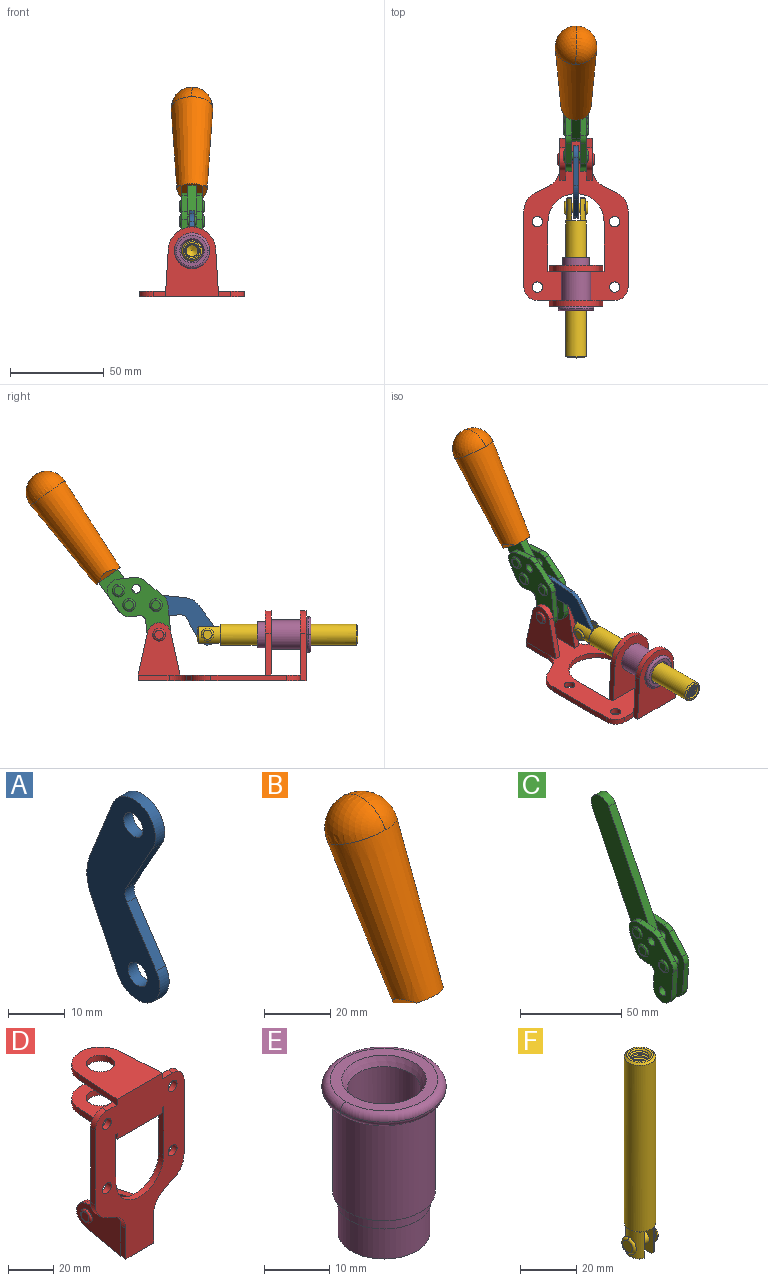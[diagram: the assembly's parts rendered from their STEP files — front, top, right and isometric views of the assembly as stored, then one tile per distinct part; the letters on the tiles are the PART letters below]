
ASSEMBLY  parts=6 mates=6
PART A: 12 faces, bbox 2.3x18.2x42.8 mm
  f0: cylinder r=2.4mm len=4.8mm, axis (1,0,0), area 34.9mm2, adj f4,f11
  f1: cylinder r=10.41mm len=8.47mm, axis (1,0,0), area 20.2mm2, adj f4,f9,f10,f11
  f2: cylinder r=3.05mm len=3.16mm, axis (1,0,0), area 7.7mm2, adj f4,f6,f7,f11
  f3: cylinder r=2.4mm len=4.8mm, axis (1,0,0), area 34.9mm2, adj f4,f11
  f4: plane 42.81x18.23mm, normal (-1,0,0), area 414.1mm2, adj f0,f1,f2,f3,f5,f6,f7,f8
  f5: cylinder r=5.54mm len=10.67mm, axis (1,0,0), area 41.8mm2, adj f4,f6,f10,f11
  f6: plane 11.66x6.53mm, normal (0,-0.87,-0.49), area 30.9mm2, adj f2,f4,f5,f11
  f7: plane 11.17x7.33mm, normal (0,-0.84,0.55), area 30.9mm2, adj f2,f4,f8,f11
  f8: cylinder r=5.54mm len=10.51mm, axis (1,0,0), area 41.8mm2, adj f4,f7,f9,f11
  f9: plane 13.67x6.67mm, normal (0,0.9,-0.44), area 35.1mm2, adj f1,f4,f8,f11
  f10: plane 14.1x5.7mm, normal (0,0.93,0.37), area 35.1mm2, adj f1,f4,f5,f11
  f11: plane 42.81x18.23mm, normal (1,0,0), area 414.1mm2, adj f0,f1,f2,f3,f5,f6,f7,f8
PART B: 11 faces, bbox 22.3x42.6x64.5 mm
  f0: sphere r=11.13mm, area 411.4mm2, adj f1,f8
  f1: cone r=11.11mm half-angle=3.3deg, axis (0,0.44,0.9), area 3251.8mm2, adj f0,f7,f8,f9,f10
  f2: cylinder r=6.16mm len=11.7mm, axis (1,0,0), area 89.5mm2, adj f3,f4,f5,f6
  f3: plane 60.23x36.75mm, normal (-1,0,0), area 763.6mm2, adj f2,f4,f6,f10
  f4: plane 51.37x25.05mm, normal (0,0.9,-0.44), area 264.2mm2, adj f2,f3,f5,f10
  f5: plane 60.23x36.75mm, normal (1,0,0), area 763.6mm2, adj f2,f4,f6,f10
  f6: plane 51.37x25.05mm, normal (0,-0.9,0.44), area 264.2mm2, adj f2,f3,f5,f10
  f7: plane 9.95x5.95mm, normal (0.71,-0.31,-0.64), area 25.8mm2, adj f1,f10
  f8: sphere r=11.13mm, area 411.4mm2, adj f0,f1
  f9: plane 9.95x5.95mm, normal (-0.71,-0.31,-0.64), area 25.8mm2, adj f1,f10
  f10: plane 14.27x11.38mm, normal (0,-0.44,-0.9), area 106.7mm2, adj f1,f3,f4,f5,f6,f7,f9
PART C: 59 faces, bbox 12.9x60.2x99.6 mm
  f0: torus R=2.39mm, axis (-1,0,0), area 14.9mm2, adj f20,f43,f51
  f1: torus R=2.39mm, axis (-1,0,0), area 14.9mm2, adj f19,f42,f51
  f2: torus R=2.39mm, axis (-1,0,0), area 14.9mm2, adj f18,f35,f51
  f3: torus R=2.39mm, axis (-1,0,0), area 14.9mm2, adj f14,f17,f23
  f4: torus R=2.39mm, axis (-1,0,0), area 14.9mm2, adj f13,f16,f23
  f5: torus R=2.39mm, axis (-1,0,0), area 14.9mm2, adj f12,f15,f23
  f6: cylinder r=2.39mm len=4.78mm, axis (1,0,0), area 46.5mm2, adj f48,f50,f51
  f7: cylinder r=2.39mm len=4.78mm, axis (1,0,0), area 46.5mm2, adj f50,f51
  f8: cylinder r=6.35mm len=12.68mm, axis (1,0,0), area 61.8mm2, adj f38,f39,f50,f51
  f9: cylinder r=2.39mm len=4.78mm, axis (-1,0,0), area 70.5mm2, adj f46,f50
  f10: cylinder r=2.39mm len=4.78mm, axis (-1,0,0), area 46.5mm2, adj f23,f45,f46
  f11: cylinder r=2.39mm len=4.78mm, axis (-1,0,0), area 46.5mm2, adj f23,f46
  f12: plane 4.78x4.78mm, normal (1,0,0), area 17.9mm2, adj f5,f15
  f13: plane 4.78x4.78mm, normal (1,0,0), area 17.9mm2, adj f4,f16
  f14: plane 4.78x4.78mm, normal (1,0,0), area 17.9mm2, adj f3,f17
  f15: torus R=2.39mm, axis (-1,0,0), area 14.9mm2, adj f5,f12,f23
  f16: torus R=2.39mm, axis (-1,0,0), area 14.9mm2, adj f4,f13,f23
  f17: torus R=2.39mm, axis (-1,0,0), area 14.9mm2, adj f3,f14,f23
  f18: plane 4.78x4.78mm, normal (-1,0,0), area 17.9mm2, adj f2,f35
  f19: plane 4.78x4.78mm, normal (-1,0,0), area 17.9mm2, adj f1,f42
  f20: plane 4.78x4.78mm, normal (-1,0,0), area 17.9mm2, adj f0,f43
  f21: plane 2.26x0.2mm, normal (1,0,0), area 0.2mm2, adj f31,f44
  f22: plane 2.26x0.2mm, normal (-1,0,0), area 0.2mm2, adj f41,f44
  f23: plane 39.37x30.77mm, normal (1,0,0), area 565.5mm2, adj f3,f4,f5,f10,f11,f15,f16,f17
  f24: cylinder r=6.1mm len=4.15mm, axis (-1,0,0), area 14.7mm2, adj f23,f25,f32,f46
  f25: plane 10.25x9.01mm, normal (0,-0.75,0.66), area 42.3mm2, adj f23,f24,f26,f46
  f26: cylinder r=6.35mm len=4.64mm, axis (-1,0,0), area 15.6mm2, adj f23,f25,f27,f46
  f27: plane 15.84x3.1mm, normal (0,-1,-0.07), area 49.2mm2, adj f23,f26,f28,f46
  f28: cylinder r=6.35mm len=12.68mm, axis (-1,0,0), area 61.8mm2, adj f23,f27,f29,f46
  f29: plane 8.11x3.1mm, normal (0,1,0.07), area 25.2mm2, adj f23,f28,f30,f46
  f30: cylinder r=3.05mm len=3.25mm, axis (-1,0,0), area 14.8mm2, adj f23,f29,f31,f46
  f31: plane 5.99x3.1mm, normal (0,0.07,-1), area 18.6mm2, adj f21,f23,f30,f44,f46
  f32: plane 9.5x3.1mm, normal (0,-0.07,1), area 29.5mm2, adj f23,f24,f33,f46,f47
  f33: cylinder r=6.1mm len=8.63mm, axis (-1,0,0), area 39.1mm2, adj f23,f32,f34,f47
  f34: plane 8.65x3.96mm, normal (0,0.91,-0.42), area 29.5mm2, adj f23,f33,f44,f47
  f35: torus R=2.39mm, axis (-1,0,0), area 14.9mm2, adj f2,f18,f51
  f36: plane 10.25x9.01mm, normal (0,-0.75,0.66), area 42.3mm2, adj f37,f49,f50,f51
  f37: cylinder r=6.35mm len=4.64mm, axis (1,0,0), area 15.6mm2, adj f36,f38,f50,f51
  f38: plane 15.84x3.1mm, normal (0,-1,-0.07), area 49.2mm2, adj f8,f37,f50,f51
  f39: plane 8.11x3.1mm, normal (0,1,0.07), area 25.2mm2, adj f8,f40,f50,f51
  f40: cylinder r=3.05mm len=3.25mm, axis (1,0,0), area 14.8mm2, adj f39,f41,f50,f51
  f41: plane 5.99x3.1mm, normal (0,0.07,-1), area 18.6mm2, adj f22,f40,f44,f50,f51
  f42: torus R=2.39mm, axis (-1,0,0), area 14.9mm2, adj f1,f19,f51
  f43: torus R=2.39mm, axis (-1,0,0), area 14.9mm2, adj f0,f20,f51
  f44: cylinder r=6.35mm len=12.12mm, axis (-1,0,0), area 128.9mm2, adj f21,f22,f23,f31,f34,f41,f46,f47
  f45: plane 2.65x1.35mm, normal (1,0,0), area 1mm2, adj f10,f55
  f46: plane 39.08x20.42mm, normal (-1,0,0), area 412.5mm2, adj f9,f10,f11,f24,f25,f26,f27,f28
  f47: plane 77.62x39.82mm, normal (1,0,0), area 850mm2, adj f32,f33,f34,f44,f53,f54,f55
  f48: plane 2.65x1.35mm, normal (-1,0,0), area 1mm2, adj f6,f55
  f49: cylinder r=6.1mm len=4.15mm, axis (1,0,0), area 14.7mm2, adj f36,f50,f51,f56
  f50: plane 39.08x20.42mm, normal (1,0,0), area 412.5mm2, adj f6,f7,f8,f9,f36,f37,f38,f39
  f51: plane 39.37x30.77mm, normal (-1,0,0), area 565.5mm2, adj f0,f1,f2,f6,f7,f8,f35,f36
  f52: plane 8.65x3.96mm, normal (0,0.91,-0.42), area 29.5mm2, adj f44,f51,f57,f58
  f53: plane 68.49x33.4mm, normal (0,0.9,-0.44), area 358.1mm2, adj f44,f47,f54,f58
  f54: cylinder r=6.35mm len=12.06mm, axis (1,0,0), area 93.7mm2, adj f47,f53,f55,f58
  f55: plane 68.49x33.4mm, normal (0,-0.9,0.44), area 358.1mm2, adj f44,f45,f46,f47,f48,f50,f54,f58
  f56: plane 9.5x3.1mm, normal (0,-0.07,1), area 29.5mm2, adj f49,f50,f51,f57,f58
  f57: cylinder r=6.1mm len=8.63mm, axis (1,0,0), area 39.1mm2, adj f51,f52,f56,f58
  f58: plane 77.62x39.82mm, normal (-1,0,0), area 850mm2, adj f44,f52,f53,f54,f55,f56,f57
PART D: 55 faces, bbox 55.7x37.4x89.8 mm
  f0: torus R=2.41mm, axis (-1,0,0), area 15mm2, adj f11,f15,f25
  f1: torus R=2.41mm, axis (-1,0,0), area 15mm2, adj f10,f12,f22
  f2: cylinder r=2.78mm len=5.56mm, axis (0,-1,0), area 54.2mm2, adj f30,f54
  f3: cylinder r=14.99mm len=29.97mm, axis (0,-1,0), area 145.9mm2, adj f30,f49,f53,f54
  f4: cylinder r=2.78mm len=5.56mm, axis (0,-1,0), area 54.2mm2, adj f30,f54
  f5: cylinder r=2.78mm len=5.56mm, axis (0,-1,0), area 54.2mm2, adj f30,f54
  f6: cylinder r=2.78mm len=5.56mm, axis (0,-1,0), area 54.2mm2, adj f30,f54
  f7: cylinder r=6.35mm len=12.7mm, axis (0,0,1), area 123.6mm2, adj f27,f51
  f8: cylinder r=6.35mm len=12.7mm, axis (0,0,-1), area 124.7mm2, adj f21,f35
  f9: cylinder r=2.41mm len=11.18mm, axis (-1,0,0), area 169.4mm2, adj f16,f19
  f10: plane 4.83x4.83mm, normal (1,0,0), area 18.3mm2, adj f1,f12
  f11: plane 4.83x4.83mm, normal (-1,0,0), area 18.3mm2, adj f0,f15
  f12: torus R=2.41mm, axis (-1,0,0), area 15mm2, adj f1,f10,f22
  f13: cylinder r=6.35mm len=12.41mm, axis (1,0,0), area 53.4mm2, adj f18,f19,f22,f23
  f14: cylinder r=6.35mm len=12.41mm, axis (-1,0,0), area 53.4mm2, adj f16,f17,f24,f25
  f15: torus R=2.41mm, axis (-1,0,0), area 15mm2, adj f0,f11,f25
  f16: plane 27.86x22.35mm, normal (1,0,0), area 425.4mm2, adj f9,f14,f17,f24,f30
  f17: plane 22.86x4.97mm, normal (0,0.21,0.98), area 72.5mm2, adj f14,f16,f25,f30
  f18: plane 22.86x4.97mm, normal (0,0.21,0.98), area 72.5mm2, adj f13,f19,f22,f30
  f19: plane 27.86x22.35mm, normal (-1,0,0), area 425.4mm2, adj f9,f13,f18,f23,f30
  f20: cylinder r=12.7mm len=25.35mm, axis (0,0,-1), area 119.8mm2, adj f21,f34,f35,f36
  f21: plane 34.21x28.07mm, normal (0,0,-1), area 702.4mm2, adj f8,f20,f30,f34,f36
  f22: plane 27.96x22.45mm, normal (1,0,0), area 407.2mm2, adj f1,f12,f13,f18,f23,f30,f42,f43
  f23: plane 22.86x4.97mm, normal (0,0.21,-0.98), area 72.5mm2, adj f13,f19,f22,f44
  f24: plane 22.86x4.97mm, normal (0,0.21,-0.98), area 72.5mm2, adj f14,f16,f25,f44
  f25: plane 27.86x22.35mm, normal (-1,0,0), area 407.1mm2, adj f0,f14,f15,f17,f24,f30,f45,f46
  f26: plane 3.1x0.95mm, normal (0,0,-1), area 2.7mm2, adj f30,f49,f50,f54
  f27: plane 34.21x28.07mm, normal (0,0,1), area 702.4mm2, adj f7,f28,f30,f50,f52
  f28: cylinder r=12.7mm len=25.35mm, axis (0,0,1), area 118.8mm2, adj f27,f50,f51,f52
  f29: plane 3.1x0.95mm, normal (0,0,-1), area 2.7mm2, adj f30,f52,f53,f54
  f30: plane 86.54x55.63mm, normal (0,1,0), area 2362.9mm2, adj f2,f3,f4,f5,f6,f16,f17,f18
  f31: plane 40.56x3.1mm, normal (-1,0,0), area 125.7mm2, adj f30,f32,f48,f54
  f32: cylinder r=7.11mm len=7.11mm, axis (0,-1,0), area 34.6mm2, adj f30,f31,f33,f54
  f33: plane 6.67x3.1mm, normal (0,0,1), area 20.4mm2, adj f30,f32,f34,f54
  f34: plane 25.39x3.13mm, normal (-1,0.06,0), area 79.5mm2, adj f20,f21,f33,f35,f54
  f35: plane 37.31x28.45mm, normal (0,0,1), area 789.9mm2, adj f8,f20,f34,f36,f54
  f36: plane 25.39x3.13mm, normal (1,0.06,0), area 79.5mm2, adj f20,f21,f35,f37,f54
  f37: plane 6.67x3.1mm, normal (0,0,1), area 20.4mm2, adj f30,f36,f38,f54
  f38: cylinder r=7.11mm len=7.11mm, axis (0,-1,0), area 34.6mm2, adj f30,f37,f39,f54
  f39: plane 40.56x3.1mm, normal (1,0,0), area 125.7mm2, adj f30,f38,f40,f54
  f40: cylinder r=11.18mm len=10.16mm, axis (0,-1,0), area 39.5mm2, adj f30,f39,f41,f54
  f41: plane 6.09x3.1mm, normal (0.42,0,-0.91), area 20.8mm2, adj f30,f40,f42,f54
  f42: cylinder r=11.18mm len=9.41mm, axis (0,-1,0), area 37.2mm2, adj f22,f30,f41,f43,f54
  f43: plane 16.5x3.1mm, normal (1,0,0), area 51.1mm2, adj f22,f42,f44,f54
  f44: plane 17.37x3.1mm, normal (0,0,-1), area 53.8mm2, adj f23,f24,f30,f43,f45,f54
  f45: plane 16.5x3.1mm, normal (-1,0,0), area 51.1mm2, adj f25,f44,f46,f54
  f46: cylinder r=11.18mm len=9.41mm, axis (0,-1,0), area 37.2mm2, adj f25,f30,f45,f47,f54
  f47: plane 6.09x3.1mm, normal (-0.42,0,-0.91), area 20.8mm2, adj f30,f46,f48,f54
  f48: cylinder r=11.18mm len=10.16mm, axis (0,-1,0), area 39.5mm2, adj f30,f31,f47,f54
  f49: plane 26.54x3.1mm, normal (-1,0,0), area 82.3mm2, adj f3,f26,f30,f54
  f50: plane 25.39x3.1mm, normal (1,0.06,0), area 78.8mm2, adj f26,f27,f28,f51,f54
  f51: plane 37.31x28.45mm, normal (0,0,-1), area 789.9mm2, adj f7,f28,f50,f52,f54
  f52: plane 25.39x3.1mm, normal (-1,0.06,0), area 78.8mm2, adj f27,f28,f29,f51,f54
  f53: plane 26.54x3.1mm, normal (1,0,0), area 82.3mm2, adj f3,f29,f30,f54
  f54: plane 89.66x55.63mm, normal (0,-1,0), area 2678.5mm2, adj f2,f3,f4,f5,f6,f26,f29,f31
PART E: 15 faces, bbox 20.6x20.6x28.7 mm
  f0: torus R=8.26mm, axis (0,0,1), area 56.8mm2, adj f1,f10,f12
  f1: torus R=8.26mm, axis (0,0,1), area 56.8mm2, adj f0,f6,f13
  f2: cylinder r=5.59mm len=25.91mm, axis (0,0,1), area 909.6mm2, adj f3,f4
  f3: cone r=6.86mm half-angle=45deg, axis (0,0,-1), area 70.2mm2, adj f2,f14
  f4: cone r=6.47mm half-angle=30deg, axis (0,0,1), area 66.7mm2, adj f2,f13
  f5: cylinder r=7.04mm len=14.07mm, axis (0,0,1), area 252.6mm2, adj f11,f14
  f6: torus R=8.26mm, axis (0,0,1), area 56.8mm2, adj f1,f12,f13
  f7: cylinder r=7.16mm len=14.33mm, axis (0,0,1), area 91.5mm2, adj f9,f11
  f8: cylinder r=7.86mm len=18.42mm, axis (0,0,1), area 909.6mm2, adj f9,f10
  f9: plane 15.72x15.72mm, normal (0,0,-1), area 33mm2, adj f7,f8
  f10: plane 16.51x16.51mm, normal (0,0,-1), area 19.9mm2, adj f0,f8,f12
  f11: plane 14.33x14.33mm, normal (0,0,-1), area 5.7mm2, adj f5,f7
  f12: torus R=8.26mm, axis (0,0,1), area 56.8mm2, adj f0,f6,f10
  f13: plane 16.51x16.51mm, normal (0,0,1), area 82.7mm2, adj f1,f4,f6
  f14: plane 14.07x14.07mm, normal (0,0,-1), area 7.8mm2, adj f3,f5
PART F: 48 faces, bbox 12.6x11.1x86.1 mm
  f0: torus R=2.41mm, axis (-1,0,0), area 15mm2, adj f30,f32,f34
  f1: torus R=2.41mm, axis (-1,0,0), area 15mm2, adj f29,f31,f33
  f2: cylinder r=5.54mm len=72.39mm, axis (0,0,1), area 2518.5mm2, adj f3,f4,f42,f43
  f3: cone r=5.54mm half-angle=45deg, axis (0,0,1), area 7.6mm2, adj f2,f5,f41
  f4: cone r=5.54mm half-angle=45deg, axis (0,0,-1), area 34.9mm2, adj f2,f39
  f5: cylinder r=5.08mm len=11.48mm, axis (0,0,1), area 108.3mm2, adj f3,f7,f8,f41
  f6: cylinder r=2.41mm len=4.83mm, axis (-1,0,0), area 71.2mm2, adj f40,f41
  f7: cylinder r=2.41mm len=4.83mm, axis (-1,0,0), area 7.6mm2, adj f5,f34
  f8: cone r=5.08mm half-angle=45deg, axis (0,0,1), area 10.6mm2, adj f5,f37,f41
  f9: cone r=3.98mm half-angle=45deg, axis (0,0,1), area 17.6mm2, adj f27,f39,f45,f46,f47
  f10: cylinder r=2.41mm len=4.83mm, axis (-1,0,0), area 7.6mm2, adj f33,f38
  f11: cylinder r=3.2mm len=6.4mm, axis (0,0,1), area 78.4mm2, adj f12,f28,f44,f45,f47
  f12: cylinder r=3.2mm len=6.4mm, axis (0,0,1), area 10.5mm2, adj f11,f13,f45,f47
  f13: cylinder r=3.2mm len=6.4mm, axis (0,0,1), area 10.5mm2, adj f12,f14,f45,f47
  f14: cylinder r=3.2mm len=6.4mm, axis (0,0,1), area 10.5mm2, adj f13,f15,f45,f47
  f15: cylinder r=3.2mm len=6.4mm, axis (0,0,1), area 10.5mm2, adj f14,f16,f45,f47
  f16: cylinder r=3.2mm len=6.4mm, axis (0,0,1), area 10.5mm2, adj f15,f17,f45,f47
  f17: cylinder r=3.2mm len=6.4mm, axis (0,0,1), area 10.5mm2, adj f16,f18,f45,f47
  f18: cylinder r=3.2mm len=6.4mm, axis (0,0,1), area 10.5mm2, adj f17,f19,f45,f47
  f19: cylinder r=3.2mm len=6.4mm, axis (0,0,1), area 10.5mm2, adj f18,f20,f45,f47
  f20: cylinder r=3.2mm len=6.4mm, axis (0,0,1), area 10.5mm2, adj f19,f21,f45,f47
  f21: cylinder r=3.2mm len=6.4mm, axis (0,0,1), area 10.5mm2, adj f20,f22,f45,f47
  f22: cylinder r=3.2mm len=6.4mm, axis (0,0,1), area 10.5mm2, adj f21,f23,f45,f47
  f23: cylinder r=3.2mm len=6.4mm, axis (0,0,1), area 10.5mm2, adj f22,f24,f45,f47
  f24: cylinder r=3.2mm len=6.4mm, axis (0,0,1), area 10.5mm2, adj f23,f25,f45,f47
  f25: cylinder r=3.2mm len=6.4mm, axis (0,0,1), area 10.5mm2, adj f24,f26,f45,f47
  f26: cylinder r=3.2mm len=6.4mm, axis (0,0,1), area 10.5mm2, adj f25,f27,f45,f47
  f27: cylinder r=3.2mm len=6.4mm, axis (0,0,1), area 7.4mm2, adj f9,f26,f45,f47
  f28: cone r=3.2mm half-angle=60deg, axis (0,0,1), area 37.2mm2, adj f11
  f29: plane 4.83x4.83mm, normal (-1,0,0), area 18.3mm2, adj f1,f31
  f30: plane 4.83x4.83mm, normal (1,0,0), area 18.3mm2, adj f0,f32
  f31: torus R=2.41mm, axis (-1,0,0), area 15mm2, adj f1,f29,f33
  f32: torus R=2.41mm, axis (-1,0,0), area 15mm2, adj f0,f30,f34
  f33: plane 6.83x6.83mm, normal (1,0,0), area 18.3mm2, adj f1,f10,f31
  f34: plane 6.83x6.83mm, normal (-1,0,0), area 18.3mm2, adj f0,f7,f32
  f35: cone r=5.08mm half-angle=45deg, axis (0,0,1), area 10.6mm2, adj f36,f38,f40
  f36: plane 7.25x1.97mm, normal (0,0,-1), area 10mm2, adj f35,f40
  f37: plane 7.25x1.97mm, normal (0,0,-1), area 10mm2, adj f8,f41
  f38: cylinder r=5.08mm len=11.48mm, axis (0,0,1), area 108.3mm2, adj f10,f35,f40,f42
  f39: plane 9.55x9.55mm, normal (0,0,1), area 22mm2, adj f4,f9
  f40: plane 12.76x10.09mm, normal (1,0,0), area 95.7mm2, adj f6,f35,f36,f38,f42,f43
  f41: plane 12.76x10.09mm, normal (-1,0,0), area 95.7mm2, adj f3,f5,f6,f8,f37,f43
  f42: cone r=5.54mm half-angle=45deg, axis (0,0,1), area 7.6mm2, adj f2,f38,f40
  f43: plane 11.07x4.7mm, normal (0,0,-1), area 50.4mm2, adj f2,f40,f41
  f44: plane 0.89x0.62mm, normal (-1,0,0), area 0.3mm2, adj f11,f45,f46,f47
  f45: bspline ~24.8x7.63mm, area 266.6mm2, adj f9,f11,f12,f13,f14,f15,f16,f17
  f46: bspline ~24.87x7.63mm, area 73.6mm2, adj f9,f44,f45,f47
  f47: bspline ~24.98x7.63mm, area 272.5mm2, adj f9,f11,f12,f13,f14,f15,f16,f17
PLACE A rot(axis=(1,0,0),121.8deg) t=(0,41.47,11.86)mm
PLACE B rot(axis=(-1,0,0),10deg) t=(0,22.57,60.49)mm
PLACE C rot(axis=(-1,0,0),10deg) t=(0,22.57,60.49)mm
PLACE D rot(axis=(1,0,0),90deg) t=(0,9.14,0)mm fixed
PLACE E rot(axis=(1,0,0),90deg) t=(0,9.14,0)mm
PLACE F rot(axis=(1,0,0),90deg) t=(0,30.82,0)mm
MATE revolute A.f5 <-> F.f6  axis (1,0,0) through (0,15.35,24.61)mm
MATE fastened C.f54 <-> B.f2  axis (1,0,0) through (0,102.04,102.1)mm
MATE revolute A.f3 <-> C.f4  axis (1,0,0) through (0,42.89,40.4)mm
MATE revolute D.f0 <-> C.f7  axis (-1,0,0) through (0,41.23,24.61)mm
MATE slider F.f2 <-> D.f7  axis (0,-1,0) through (0,-27.96,24.61)mm
MATE fastened D.f7 <-> E.f0  axis (0,-1,0) through (0,-37.25,24.61)mm
